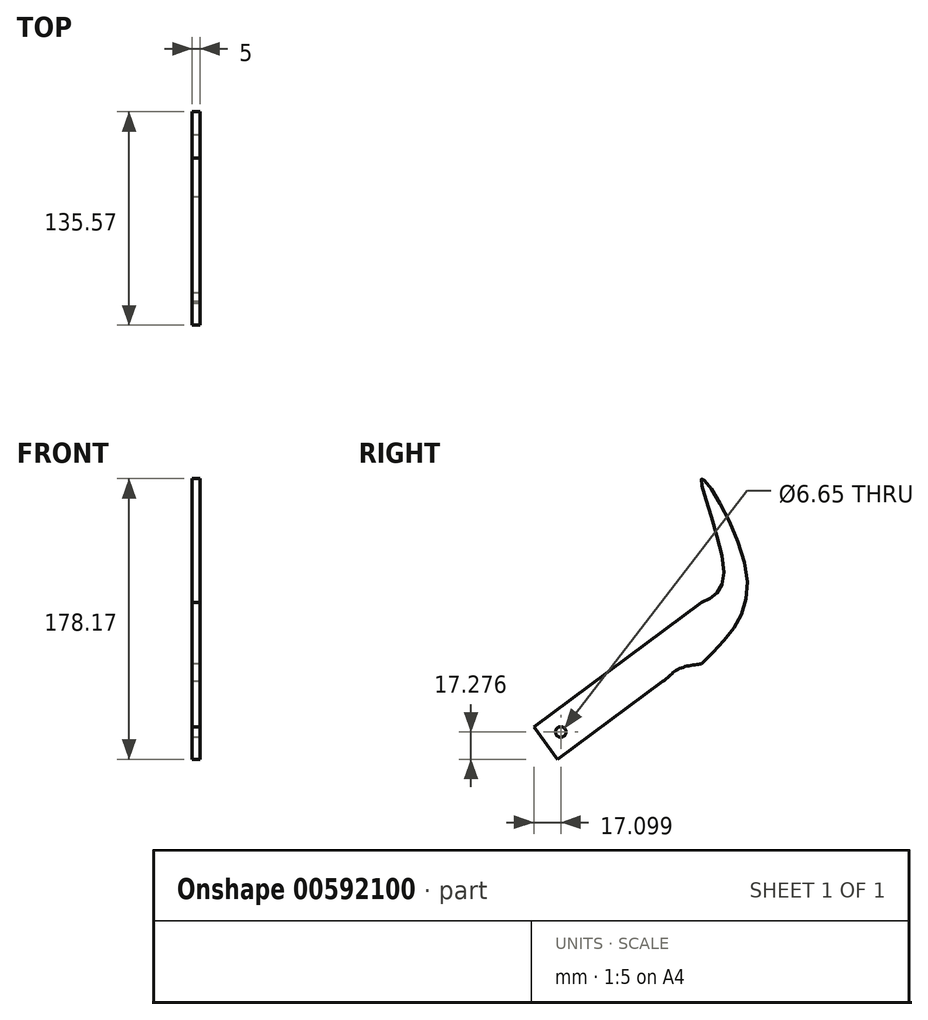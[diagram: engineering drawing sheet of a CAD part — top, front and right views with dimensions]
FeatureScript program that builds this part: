
annotation { "Feature Type Name" : "Feature", "Feature Type Description" : "" }
export const myFeature = defineFeature(function(context is Context, id is Id, definition is map)
    precondition{}
    {
        {
            var Q0;
            Q0=qCreatedBy(makeId("Right.planeOp"),FACE);
            var sketch = newSketch(context, id + "F0", { "sketchPlane" : qUnion([Q0])});
            skFitSpline(sketch, "E0", {"points": [v(0, -55.9) * mm, v(28.79, 0) * mm, v(0, 61.5) * mm, v(14.2, 0) * mm, v(0, -17.01) * mm], "startDerivative": vector(173.04, 165.43) * mm, "endDerivative": vector(-125.95, -56.55) * mm});
            skLineSegment(sketch, "E1", {"start": v(0, -17.01) * mm, "end": v(0, -55.9) * mm});
            skLineSegment(sketch, "E2", {"start": v(0, -17.01) * mm, "end": v(-106.43, -96.13) * mm});
            skLineSegment(sketch, "E3", {"start": v(-106.43, -96.13) * mm, "end": v(-91.28, -116.52) * mm});
            skLineSegment(sketch, "E4", {"start": v(-91.28, -116.52) * mm, "end": v(-24.88, -67.16) * mm});
            skFitSpline(sketch, "E5", {"points": [v(-24.88, -67.16) * mm, v(-17.04, -60.8) * mm, v(-8.04, -57.17) * mm, v(0, -55.9) * mm], "startDerivative": vector(32.33, 17.95) * mm, "endDerivative": vector(18.24, 4.77) * mm});
            skCircle(sketch, "E6", {"center": v(-89.33, -99.24) * mm, "radius": 3.33 * mm});
            skSolve(sketch);
        }
        {
            var Q0;
            Q0=makeQuery(id+"F0.imprint","IMPRINT",FACE,{"disambiguationData":[TD([[makeQuery(id+"F0.imprint","IMPRINT",EDGE,{"derivedFrom":sQuery(id+"F0.wireOp",EDGE,"E0")}),1.0]])]});
            var Q1;
            Q1=makeQuery(id+"F0.imprint","IMPRINT",FACE,{"disambiguationData":[TD([[makeQuery(id+"F0.imprint","IMPRINT",EDGE,{"derivedFrom":sQuery(id+"F0.wireOp",EDGE,"E1")}),-1.0]])]});
            extrude(context, id + "F1", {"entities" : qUnion([Q0, Q1]), "depth" : 5 * mm, "offsetDistance" : 25.4 * mm});
        }
    });
